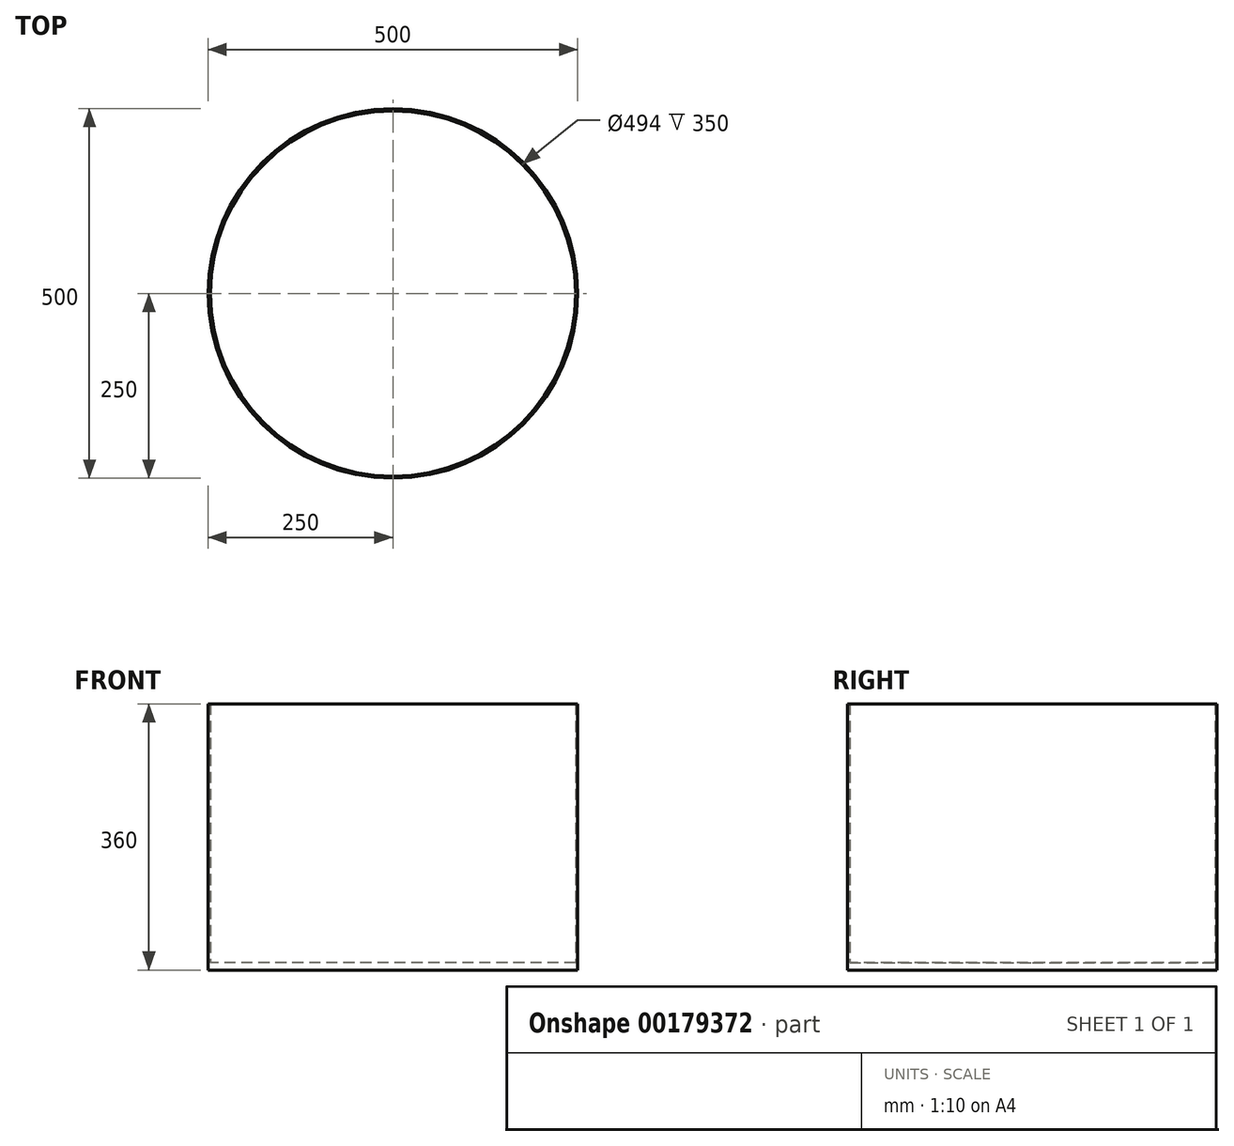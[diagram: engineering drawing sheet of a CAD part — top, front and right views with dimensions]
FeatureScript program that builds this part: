
annotation { "Feature Type Name" : "Feature", "Feature Type Description" : "" }
export const myFeature = defineFeature(function(context is Context, id is Id, definition is map)
    precondition{}
    {
        {
            var Q0;
            Q0=qCreatedBy(makeId("Top.planeOp"),FACE);
            var sketch = newSketch(context, id + "F0", { "sketchPlane" : qUnion([Q0])});
            skCircle(sketch, "E0", {"center": v(0, 0) * mm, "radius": 250 * mm});
            skSolve(sketch);
        }
        {
            var Q0;
            Q0 = qSketchRegion(id + "F0", true);
            extrude(context, id + "F1", {"entities" : qUnion([Q0]), "depth" : 10 * mm});
        }
        {
            var Q0;
            Q0=makeQuery(id+"F1.opExtrude","CAP_FACE",FACE,{"disambiguationData":[OSD([sQuery(id+"F0.wireOp",EDGE,"E0")])],"isStart":false});
            var sketch = newSketch(context, id + "F2", { "sketchPlane" : qUnion([Q0])});
            skCircle(sketch, "E1", {"center": v(0, 0) * mm, "radius": 247 * mm});
            skLineSegment(sketch, "E2", {"start": v(247, 0) * mm, "end": v(250, 0) * mm, "construction": true});
            skSolve(sketch);
        }
        {
            var Q0;
            Q0=makeQuery(id+"F2.imprint","IMPRINT",FACE,{"disambiguationData":[TD([[makeQuery(id+"F2.imprint","IMPRINT",EDGE,{"derivedFrom":sQuery(id+"F2.wireOp",EDGE,"E1")}),-1.0]])]});
            extrude(context, id + "F3", {"entities" : qUnion([Q0]), "operationType" : NewBodyOperationType.ADD, "depth" : 350 * mm});
        }
    });
